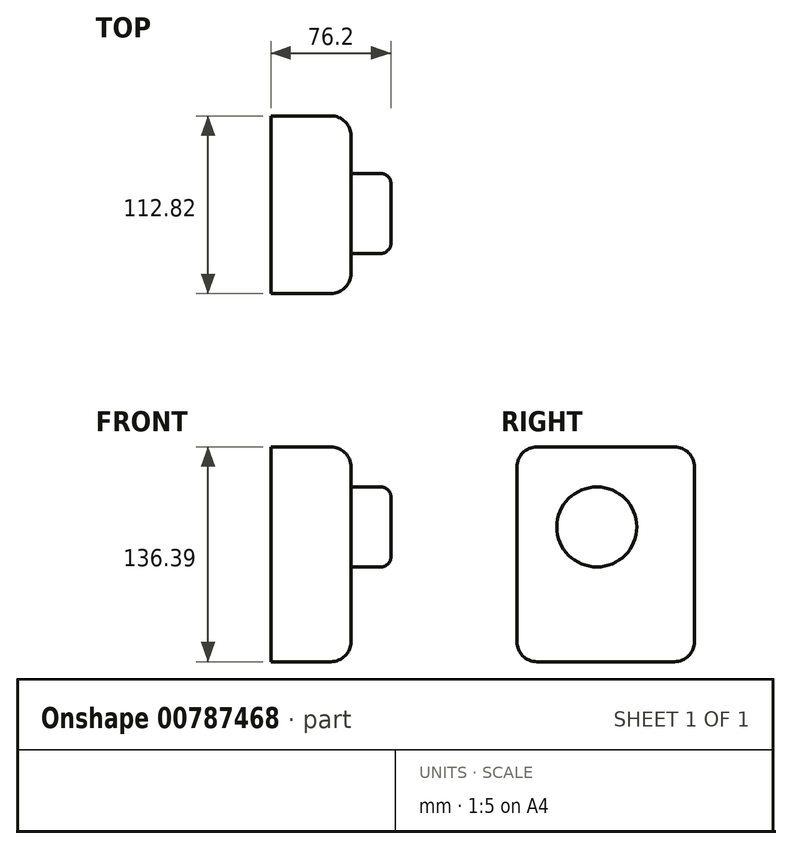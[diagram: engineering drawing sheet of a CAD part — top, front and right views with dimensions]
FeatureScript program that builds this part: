
annotation { "Feature Type Name" : "Feature", "Feature Type Description" : "" }
export const myFeature = defineFeature(function(context is Context, id is Id, definition is map)
    precondition{}
    {
        {
            var Q0;
            Q0=qCreatedBy(makeId("Top.planeOp"),FACE);
            var sketch = newSketch(context, id + "F0", { "sketchPlane" : qUnion([Q0])});
            skLineSegment(sketch, "E0.bottom", {"start": v(0, 0) * mm, "end": v(50.8, 0) * mm});
            skLineSegment(sketch, "E0.top", {"start": v(0, 112.82) * mm, "end": v(50.8, 112.82) * mm});
            skLineSegment(sketch, "E0.left", {"start": v(0, 0) * mm, "end": v(0, 112.82) * mm});
            skLineSegment(sketch, "E0.right", {"start": v(50.8, 0) * mm, "end": v(50.8, 112.82) * mm});
            skSolve(sketch);
        }
        {
            var Q0;
            Q0=makeQuery(id+"F0.imprint","IMPRINT",FACE,{"disambiguationData":[TD([[makeQuery(id+"F0.imprint","IMPRINT",EDGE,{"derivedFrom":sQuery(id+"F0.wireOp",EDGE,"E0.bottom")}),1.0]])]});
            extrude(context, id + "F1", {"entities" : qUnion([Q0]), "depth" : 136.39 * mm, "offsetDistance" : 25.4 * mm});
        }
        {
            var Q0;
            Q0=makeQuery(id+"F1.opExtrude","SWEPT_FACE",FACE,{"disambiguationData":[OSD([sQuery(id+"F0.wireOp",EDGE,"E0.right")])]});
            var sketch = newSketch(context, id + "F2", { "sketchPlane" : qUnion([Q0])});
            skCircle(sketch, "E1", {"center": v(50.8, 85.59) * mm, "radius": 25.4 * mm});
            skSolve(sketch);
        }
        {
            var Q0;
            Q0 = qSketchRegion(id + "F2", true);
            extrude(context, id + "F3", {"entities" : qUnion([Q0]), "operationType" : NewBodyOperationType.ADD, "depth" : 25.4 * mm, "offsetDistance" : 25.4 * mm});
        }
        {
            var Q0;
            Q0=makeQuery(id+"F3.opExtrude","CAP_EDGE",EDGE,{"disambiguationData":[OSD([sQuery(id+"F2.wireOp",EDGE,"E1")])],"isStart":false});
            var Q1;
            Q1=makeQuery(id+"F3.opExtrude","CAP_EDGE",EDGE,{"disambiguationData":[OSD([sQuery(id+"F2.wireOp",EDGE,"E1")])],"isStart":true});
            fillet(context, id + "F4", {"entities" : qUnion([Q0, Q1]), "radius" : 6.35 * mm, "tangentPropagation" : true, "allowEdgeOverflow" : false});
        }
        {
            var Q0;
            Q0=makeQuery(id+"F1.opExtrude","CAP_EDGE",EDGE,{"disambiguationData":[OSD([sQuery(id+"F0.wireOp",EDGE,"E0.top")])],"isStart":false});
            var Q1;
            Q1=makeQuery(id+"F1.opExtrude","CAP_EDGE",EDGE,{"disambiguationData":[OSD([sQuery(id+"F0.wireOp",EDGE,"E0.top")])],"isStart":true});
            var Q2;
            Q2=makeQuery(id+"F1.opExtrude","CAP_EDGE",EDGE,{"disambiguationData":[OSD([sQuery(id+"F0.wireOp",EDGE,"E0.bottom")])],"isStart":true});
            var Q3;
            Q3=makeQuery(id+"F1.opExtrude","CAP_EDGE",EDGE,{"disambiguationData":[OSD([sQuery(id+"F0.wireOp",EDGE,"E0.bottom")])],"isStart":false});
            fillet(context, id + "F5", {"entities" : qUnion([Q0, Q1, Q2, Q3]), "radius" : 12.7 * mm, "tangentPropagation" : true, "allowEdgeOverflow" : false});
        }
        {
            var Q0;
            Q0=makeQuery(id+"F1.opExtrude","SWEPT_EDGE",EDGE,{"disambiguationData":[OSD([sQuery(id+"F0.wireOp",EDGE,"E0.bottom"),sQuery(id+"F0.wireOp",EDGE,"E0.right")])]});
            fillet(context, id + "F6", {"entities" : qUnion([Q0]), "radius" : 12.7 * mm, "tangentPropagation" : true, "allowEdgeOverflow" : false});
        }
    });
